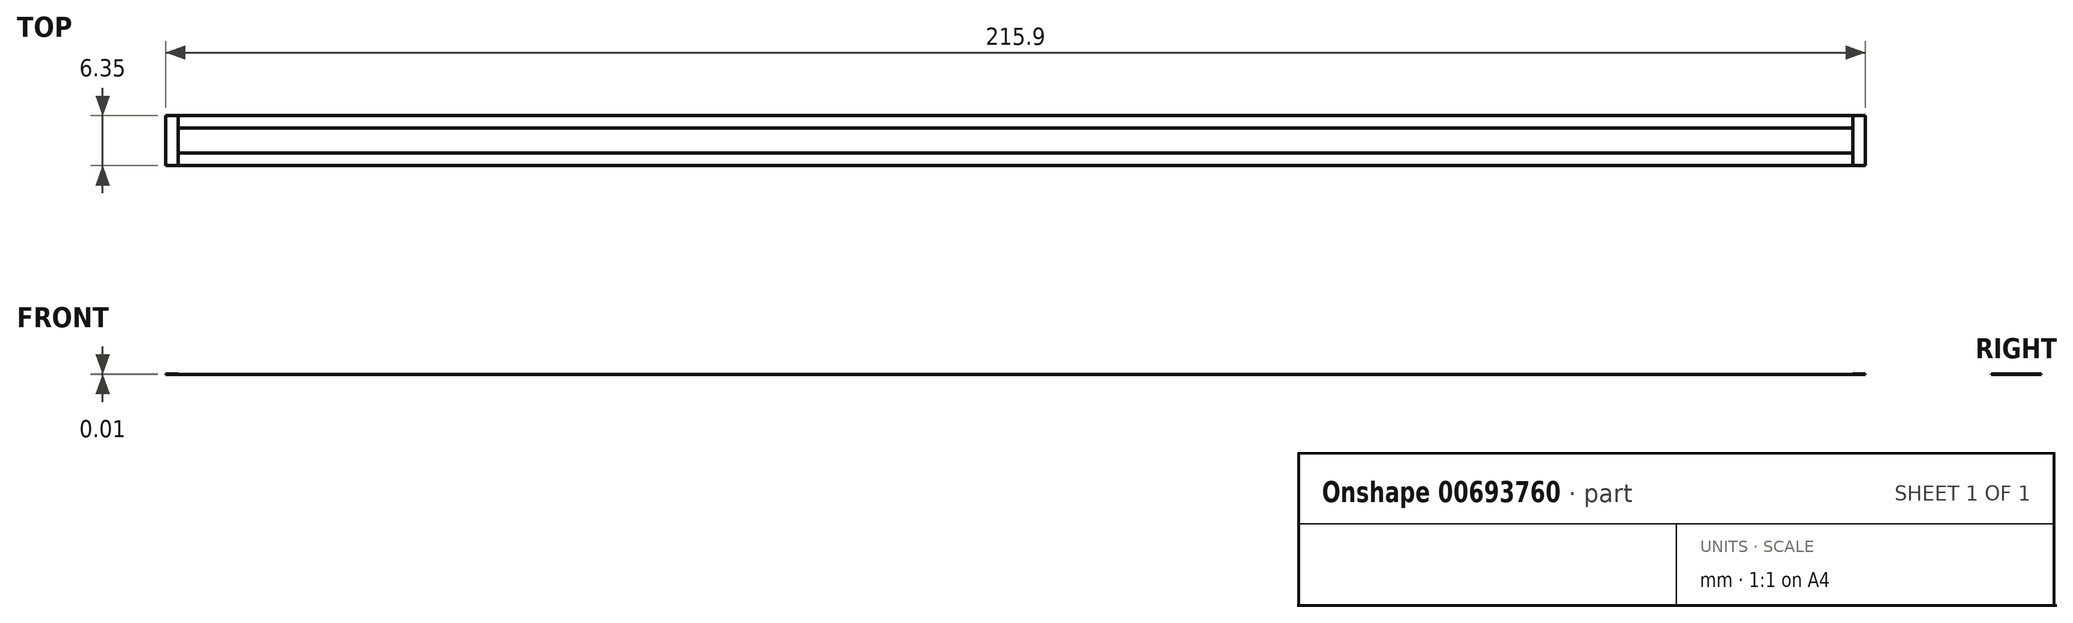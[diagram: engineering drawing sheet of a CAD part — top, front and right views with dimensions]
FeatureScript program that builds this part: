
annotation { "Feature Type Name" : "Feature", "Feature Type Description" : "" }
export const myFeature = defineFeature(function(context is Context, id is Id, definition is map)
    precondition{}
    {
        {
            var Q0;
            Q0=qCreatedBy(makeId("Top.planeOp"),FACE);
            var sketch = newSketch(context, id + "F0", { "sketchPlane" : qUnion([Q0])});
            skLineSegment(sketch, "E0.bottom", {"start": v(0, 0) * mm, "end": v(215.9, 0) * mm});
            skLineSegment(sketch, "E0.top", {"start": v(0, 6.35) * mm, "end": v(215.9, 6.35) * mm});
            skLineSegment(sketch, "E0.left", {"start": v(0, 0) * mm, "end": v(0, 6.35) * mm});
            skLineSegment(sketch, "E0.right", {"start": v(215.9, 0) * mm, "end": v(215.9, 6.35) * mm});
            skLineSegment(sketch, "E1.bottom", {"start": v(1.59, 1.59) * mm, "end": v(214.31, 1.59) * mm});
            skLineSegment(sketch, "E1.top", {"start": v(1.59, 4.76) * mm, "end": v(214.31, 4.76) * mm});
            skLineSegment(sketch, "E1.left", {"start": v(1.59, 1.59) * mm, "end": v(1.59, 4.76) * mm});
            skLineSegment(sketch, "E1.right", {"start": v(214.31, 1.59) * mm, "end": v(214.31, 4.76) * mm});
            skLineSegment(sketch, "E2", {"start": v(214.31, 4.76) * mm, "end": v(214.31, 6.35) * mm, "construction": true});
            skLineSegment(sketch, "E3", {"start": v(214.31, 4.76) * mm, "end": v(215.9, 4.76) * mm, "construction": true});
            skLineSegment(sketch, "E4", {"start": v(1.59, 1.59) * mm, "end": v(1.59, 0) * mm, "construction": true});
            skLineSegment(sketch, "E5", {"start": v(1.59, 1.59) * mm, "end": v(0, 1.59) * mm, "construction": true});
            skSolve(sketch);
        }
        {
            var Q0;
            Q0=makeQuery(id+"F0.imprint","IMPRINT",FACE,{"disambiguationData":[TD([[makeQuery(id+"F0.imprint","IMPRINT",EDGE,{"derivedFrom":sQuery(id+"F0.wireOp",EDGE,"E0.bottom")}),1.0]])]});
            extrude(context, id + "F1", {"entities" : qUnion([Q0]), "depth" : 1 / 203.2 * mm, "offsetDistance" : 25.4 * mm});
        }
        {
            var Q0;
            Q0=makeQuery(id+"F1.opExtrude","CAP_FACE",FACE,{"disambiguationData":[OSD([sQuery(id+"F0.wireOp",EDGE,"E0.bottom"),sQuery(id+"F0.wireOp",EDGE,"E0.top"),sQuery(id+"F0.wireOp",EDGE,"E0.left"),sQuery(id+"F0.wireOp",EDGE,"E0.right"),sQuery(id+"F0.wireOp",EDGE,"E1.bottom"),sQuery(id+"F0.wireOp",EDGE,"E1.top"),sQuery(id+"F0.wireOp",EDGE,"E1.left"),sQuery(id+"F0.wireOp",EDGE,"E1.right")])],"isStart":false});
            var sketch = newSketch(context, id + "F2", { "sketchPlane" : qUnion([Q0])});
            skLineSegment(sketch, "E6.0", {"start": v(214.31, 1.59) * mm, "end": v(214.31, 4.76) * mm});
            skLineSegment(sketch, "E7.0", {"start": v(215.9, 0) * mm, "end": v(215.9, 6.35) * mm});
            skLineSegment(sketch, "E8.bottom", {"start": v(215.9, 6.35) * mm, "end": v(214.31, 6.35) * mm});
            skLineSegment(sketch, "E8.top", {"start": v(215.9, 0) * mm, "end": v(214.31, 0) * mm});
            skLineSegment(sketch, "E8.left", {"start": v(215.9, 6.35) * mm, "end": v(215.9, 0) * mm});
            skLineSegment(sketch, "E8.right", {"start": v(214.31, 6.35) * mm, "end": v(214.31, 0) * mm});
            skLineSegment(sketch, "E9.0", {"start": v(0, 0) * mm, "end": v(0, 6.35) * mm});
            skLineSegment(sketch, "E10.0", {"start": v(1.59, 1.59) * mm, "end": v(1.59, 4.76) * mm});
            skLineSegment(sketch, "E11.bottom", {"start": v(0, 6.35) * mm, "end": v(1.59, 6.35) * mm});
            skLineSegment(sketch, "E11.top", {"start": v(0, 0) * mm, "end": v(1.59, 0) * mm});
            skLineSegment(sketch, "E11.left", {"start": v(0, 6.35) * mm, "end": v(0, 0) * mm});
            skLineSegment(sketch, "E11.right", {"start": v(1.59, 6.35) * mm, "end": v(1.59, 0) * mm});
            skSolve(sketch);
        }
        {
            var Q0;
            {var subQ2=sQuery(id+"F2.wireOp",EDGE,"E11.bottom");Q0=makeQuery(id+"F2.imprint","IMPRINT",FACE,{"disambiguationData":[TD([[makeQuery(id+"F2.imprint","IMPRINT",EDGE,{"derivedFrom":subQ2}),-1.0]])]});}
            var Q1;
            {var subQ2=sQuery(id+"F2.wireOp",EDGE,"E8.bottom");Q1=makeQuery(id+"F2.imprint","IMPRINT",FACE,{"disambiguationData":[TD([[makeQuery(id+"F2.imprint","IMPRINT",EDGE,{"derivedFrom":subQ2}),-1.0]])]});}
            extrude(context, id + "F3", {"entities" : qUnion([Q0, Q1]), "operationType" : NewBodyOperationType.ADD, "depth" : 1 / 203.2 * mm, "offsetDistance" : 25.4 * mm});
        }
    });
